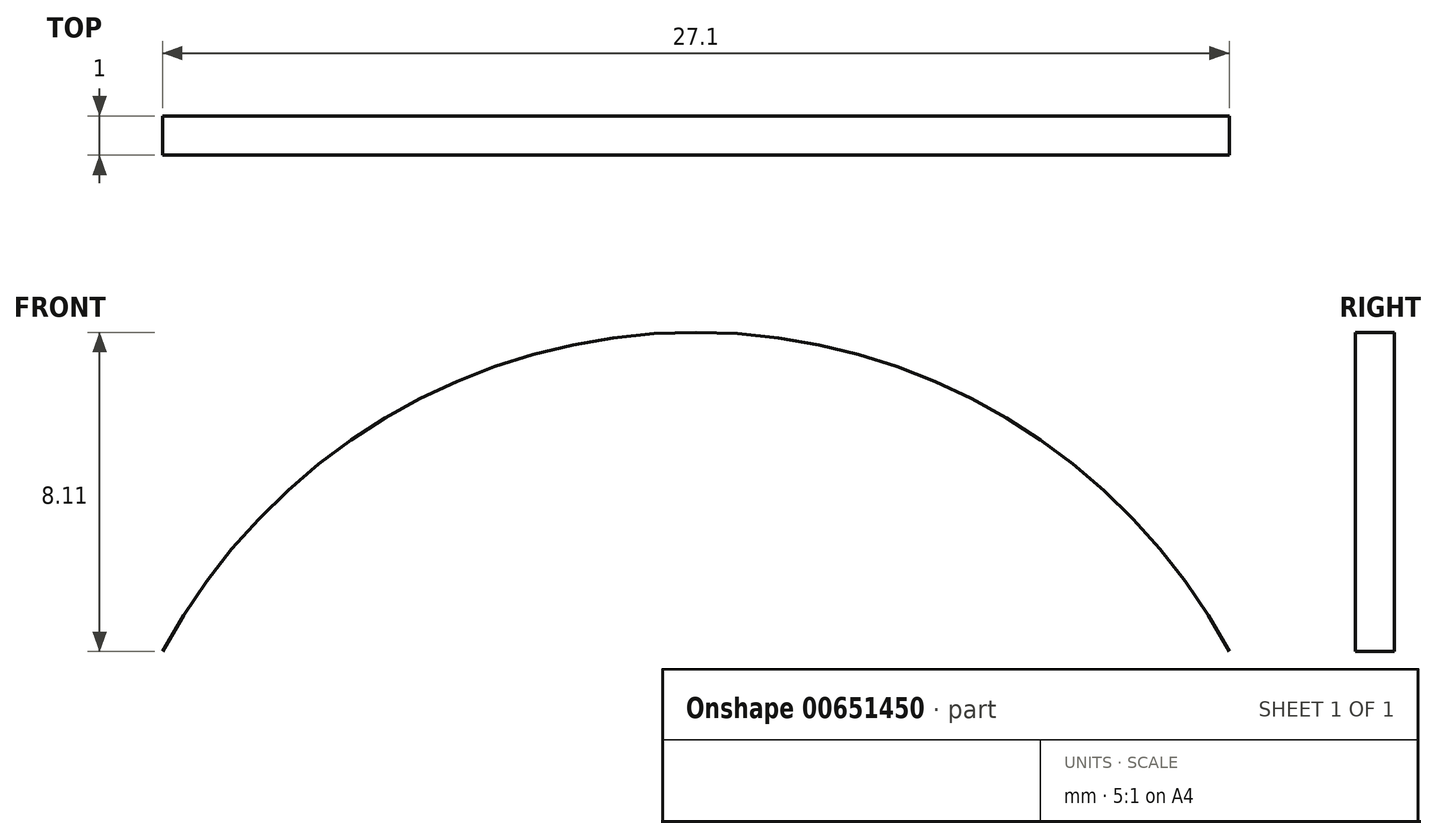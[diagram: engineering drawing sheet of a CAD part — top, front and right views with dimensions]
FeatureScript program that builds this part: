
annotation { "Feature Type Name" : "Feature", "Feature Type Description" : "" }
export const myFeature = defineFeature(function(context is Context, id is Id, definition is map)
    precondition{}
    {
        {
            var Q0;
            Q0=qCreatedBy(makeId("Front.planeOp"),FACE);
            var sketch = newSketch(context, id + "F0", { "sketchPlane" : qUnion([Q0])});
            skArc(sketch, "E0", {"start": v(13.55, 0) * mm, "mid": v(0, 8.11) * mm, "end": v(-13.55, 0) * mm});
            skSolve(sketch);
        }
        {
            var Q0;
            Q0=sQuery(id+"F0.wireOp",EDGE,"E0");
            extrude(context, id + "F1", {"bodyType" : ToolBodyType.SURFACE, "surfaceEntities" : qUnion([Q0]), "depth" : 1 * mm, "offsetDistance" : 25.4 * mm});
        }
    });
